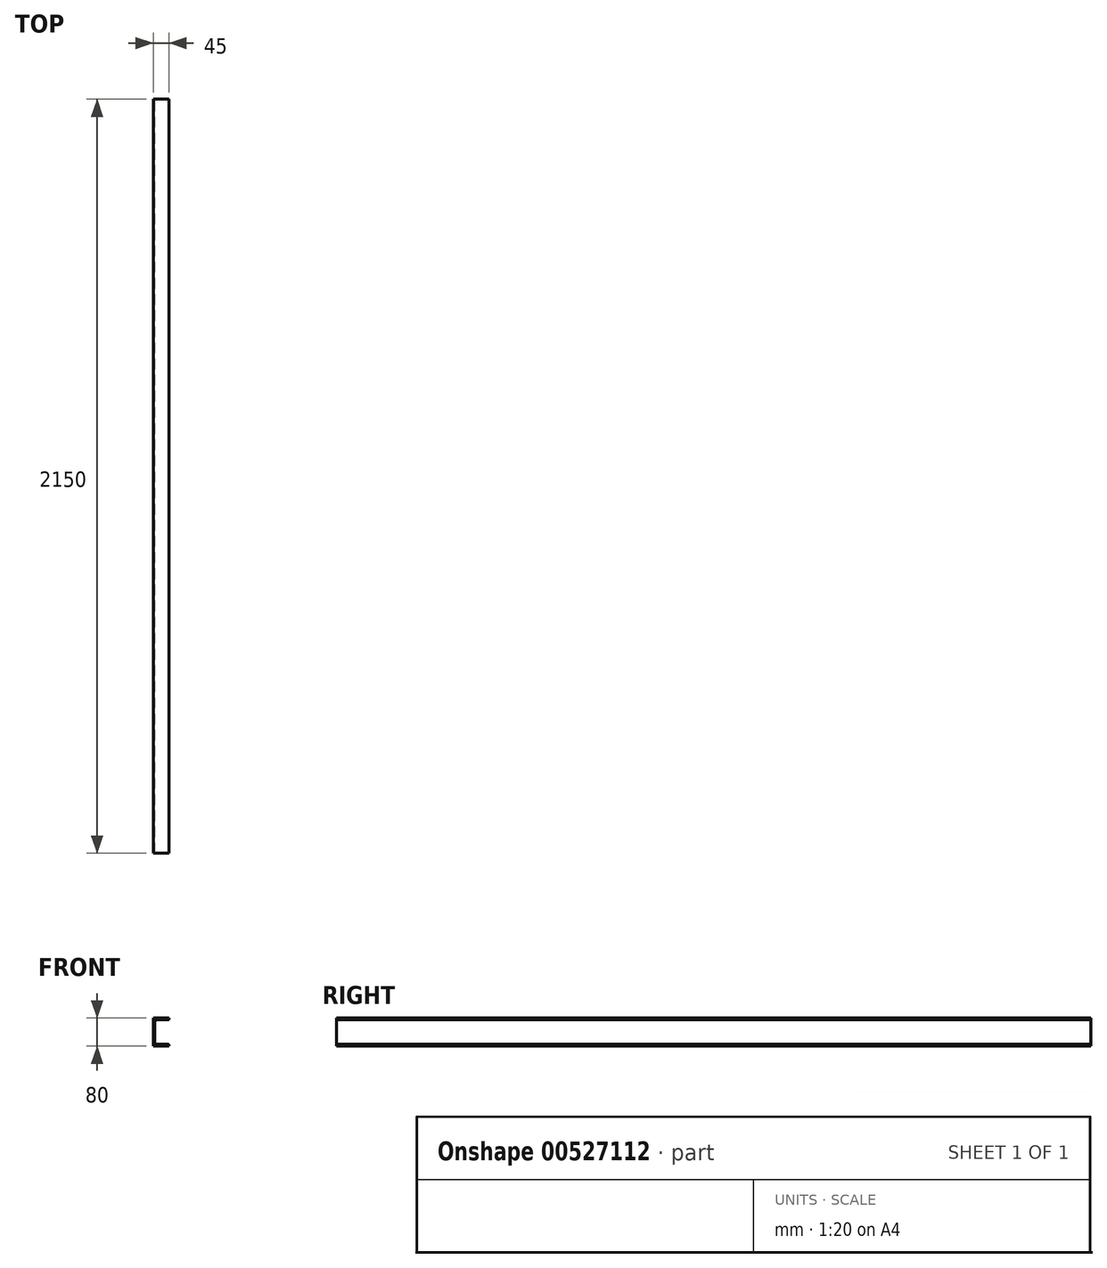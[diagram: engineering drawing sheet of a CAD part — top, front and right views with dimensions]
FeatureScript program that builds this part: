
annotation { "Feature Type Name" : "Feature", "Feature Type Description" : "" }
export const myFeature = defineFeature(function(context is Context, id is Id, definition is map)
    precondition{}
    {
        {
            var Q0;
            Q0=qCreatedBy(makeId("Front.planeOp"),FACE);
            var sketch = newSketch(context, id + "F0", { "sketchPlane" : qUnion([Q0])});
            skLineSegment(sketch, "E0.bottom", {"start": v(0, 0) * mm, "end": v(45, 0) * mm});
            skLineSegment(sketch, "E0.top", {"start": v(0, 80) * mm, "end": v(45, 80) * mm});
            skLineSegment(sketch, "E0.left", {"start": v(0, 0) * mm, "end": v(0, 80) * mm});
            skLineSegment(sketch, "E0.right", {"start": v(45, 0) * mm, "end": v(45, 3) * mm});
            skLineSegment(sketch, "E1.0", {"start": v(10, 75) * mm, "end": v(43, 75) * mm});
            skLineSegment(sketch, "E2.0", {"start": v(5, 10) * mm, "end": v(5, 70) * mm});
            skLineSegment(sketch, "E3.0", {"start": v(10, 5) * mm, "end": v(43, 5) * mm});
            skLineSegment(sketch, "E4.trimOffspring", {"start": v(45, 77) * mm, "end": v(45, 80) * mm});
            skPoint(sketch, "E5.visualSharp", {"position": v(5, 5) * mm});
            skArc(sketch, "E5.filletArc", {"start": v(5, 10) * mm, "mid": v(6.46, 6.46) * mm, "end": v(10, 5) * mm});
            skPoint(sketch, "E6.visualSharp", {"position": v(5, 75) * mm});
            skArc(sketch, "E6.filletArc", {"start": v(10, 75) * mm, "mid": v(6.46, 73.54) * mm, "end": v(5, 70) * mm});
            skPoint(sketch, "E7.visualSharp", {"position": v(45, 75) * mm});
            skArc(sketch, "E7.filletArc", {"start": v(43, 75) * mm, "mid": v(44.41, 75.59) * mm, "end": v(45, 77) * mm});
            skPoint(sketch, "E8.visualSharp", {"position": v(45, 5) * mm});
            skArc(sketch, "E8.filletArc", {"start": v(45, 3) * mm, "mid": v(44.41, 4.41) * mm, "end": v(43, 5) * mm});
            skSolve(sketch);
        }
        {
            var Q0;
            Q0=makeQuery(id+"F0.imprint","IMPRINT",FACE,{"disambiguationData":[TD([[makeQuery(id+"F0.imprint","IMPRINT",EDGE,{"derivedFrom":sQuery(id+"F0.wireOp",EDGE,"E0.bottom")}),1.0]])]});
            extrude(context, id + "F1", {"entities" : qUnion([Q0]), "depth" : 2150 * mm, "offsetDistance" : 25 * mm});
        }
    });
